# Revit family: CENTUM Dachdurchführung 89 m.Halteprofil XL100 (L=300mm bis 500mm) 166215000 bis166215004
name_source: partatom
category: HLS-Bauteile
revit_build: Autodesk Revit 2018 (Build: 20190510_1515(x64)
units: mm (PartAtom-declared; Revit-internal decimal feet)

## family parameters
Arbeitsebenenbasiert = Ja
Beim Laden mit Abzugskörper schneiden = Nein
Bemaßung runder Anschluss = Durchmesser verwenden
Gemeinsam genutzt = Ja
Immer vertikal = Nein
Raumberechnungspunkt = Nein
Teiletyp = Normal

## types (5) — shared parameters
Abmessung Grundplatte = 220x220x12 mm
Ausführung = ohne Höhenverstellung
Breite Platte = 220 mm  [stored 0.721785 ft]
EAN = 4250928455857
Fabrikat = MEFA
Firma = MEFA Befestigungs- und Montagesysteme GmbH
Gewicht = 10.81 kg
Gewicht pro Bauteil = 10.81 kg
Kurztext1 = Dachdurchführung CENTUM
Kurztext2 = für XL100 500 mm ohne Höhenverstellung
Länge = 500 mm  [stored 1.64042 ft]
Länge 1 = 510 mm
Länge Platte = 220 mm  [stored 0.721785 ft]
Material = Stahl
Oberflaeche = feuerstückverzinkt
Platte = Platte 220x220x12 18x27
Profil = CENTUM
Profiltyp = XL100
Stärke Platte = 12 mm  [stored 0.0393701 ft]
Vorgabe-Ansicht = 1219 mm
max. zul. Last Druck = 0.00 kN
zero-valued in all types: Sicherheitsfaktor, max. Profilhöhe

## per-type parameters (varying)
| type | Artikelnummer | L | Rohrlänge |
| CENTUM Dachdurchführung 88,9 m.Halteprofil XL100_ L= 350 mm | 166215001 | 350 mm  [stored 1.14829 ft] | Rohre 88.9x3.2 300 bis 500 : Rohr  88,9/3,2 L= 350 (00096831/0350) |
| CENTUM Dachdurchführung 88,9 m.Halteprofil XL100_ L= 400 mm | 166215002 | 400 mm  [stored 1.31234 ft] | Rohre 88.9x3.2 300 bis 500 : Rohr  88,9/3,2 L= 400 (00096831/0400) |
| CENTUM Dachdurchführung 88,9 m.Halteprofil XL100_ L= 450 mm | 166215003 | 450 mm  [stored 1.47638 ft] | Rohre 88.9x3.2 300 bis 500 : Rohr  88,9/3,2 L= 450 (00096831/0450) |
| CENTUM Dachdurchführung 88,9 m.Halteprofil XL100_ L= 500 mm | 166215004 | 500 mm  [stored 1.64042 ft] | Rohre 88.9x3.2 300 bis 500 : Rohr  88,9/3,2 L= 500 (00096831/0500) |
| CENTUM Dachdurchführung 88,9 m.Halteprofil XL100_ L= 300 mm | 166215000 | 300 mm  [stored 0.984252 ft] | Rohre 88.9x3.2 300 bis 500 : Rohr  88,9/3,2 L= 300 (00096831/0300) |

note: [stored X ft] marks values corroborated as IEEE doubles in the binary element streams (Revit-internal decimal feet)
